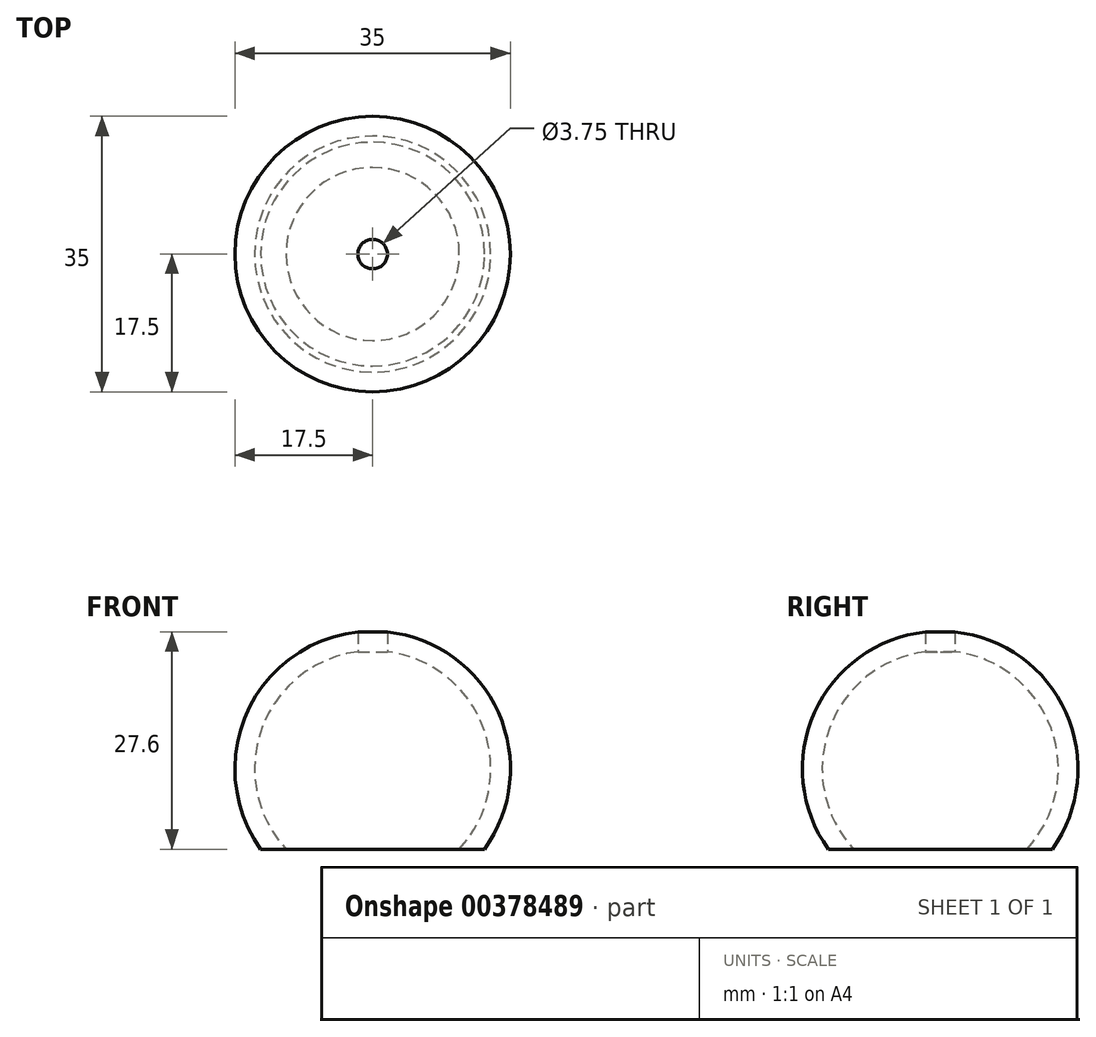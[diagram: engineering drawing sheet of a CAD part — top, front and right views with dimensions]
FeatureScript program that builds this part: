
annotation { "Feature Type Name" : "Feature", "Feature Type Description" : "" }
export const myFeature = defineFeature(function(context is Context, id is Id, definition is map)
    precondition{}
    {
        {
            var Q0;
            Q0=qCreatedBy(makeId("Front.planeOp"),FACE);
            var sketch = newSketch(context, id + "F0", { "sketchPlane" : qUnion([Q0])});
            skArc(sketch, "E0", {"start": v(0, -17.5) * mm, "mid": v(17.5, 0) * mm, "end": v(0, 17.5) * mm});
            skLineSegment(sketch, "E1", {"start": v(0, 0) * mm, "end": v(0, -17.5) * mm});
            skLineSegment(sketch, "E2", {"start": v(0, 0) * mm, "end": v(0, 17.5) * mm});
            skSolve(sketch);
        }
        {
            var Q0;
            Q0=makeQuery(id+"F0.imprint","IMPRINT",FACE,{"disambiguationData":[TD([[makeQuery(id+"F0.imprint","IMPRINT",EDGE,{"derivedFrom":sQuery(id+"F0.wireOp",EDGE,"E0")}),1.0]])]});
            var Q1;
            Q1=sQuery(id+"F0.wireOp",EDGE,"E1");
            revolve(context, id + "F1", {"entities" : qUnion([Q0]), "axis" : qUnion([Q1]), "revolveType" : RevolveType.FULL});
        }
        {
            var Q0;
            Q0=qCreatedBy(makeId("Front.planeOp"),FACE);
            var sketch = newSketch(context, id + "F2", { "sketchPlane" : qUnion([Q0])});
            skArc(sketch, "E3", {"start": v(0, -15) * mm, "mid": v(15, 0) * mm, "end": v(0, 15) * mm});
            skLineSegment(sketch, "E4", {"start": v(0, 15) * mm, "end": v(0, -15) * mm});
            skSolve(sketch);
        }
        {
            var Q0;
            Q0=makeQuery(id+"F2.imprint","IMPRINT",FACE,{"disambiguationData":[TD([[makeQuery(id+"F2.imprint","IMPRINT",EDGE,{"derivedFrom":sQuery(id+"F2.wireOp",EDGE,"E3")}),1.0]])]});
            var Q1;
            Q1=sQuery(id+"F0.wireOp",EDGE,"E2");
            revolve(context, id + "F3", {"entities" : qUnion([Q0]), "axis" : qUnion([Q1]), "revolveType" : RevolveType.FULL});
        }
        {
            var Q0;
            Q0=makeQuery(id+"F3.opRevolve","SWEPT_BODY",BODY,{"disambiguationData":[OSD([sQuery(id+"F2.wireOp",EDGE,"E3"),sQuery(id+"F2.wireOp",EDGE,"E4")])]});
            var Q1;
            Q1=makeQuery(id+"F1.opRevolve","SWEPT_BODY",BODY,{"disambiguationData":[OSD([sQuery(id+"F0.wireOp",EDGE,"E0"),sQuery(id+"F0.wireOp",EDGE,"E1"),sQuery(id+"F0.wireOp",EDGE,"E2")])]});
            booleanBodies(context, id + "F4", {"operationType" : BooleanOperationType.SUBTRACTION, "tools" : qUnion([Q0]), "targets" : qUnion([Q1])});
        }
        {
            var Q0;
            Q0=qCreatedBy(makeId("Front.planeOp"),FACE);
            var sketch = newSketch(context, id + "F5", { "sketchPlane" : qUnion([Q0])});
            skLineSegment(sketch, "E5.bottom", {"start": v(-19.8, -21) * mm, "end": v(22.47, -21) * mm});
            skLineSegment(sketch, "E5.top", {"start": v(-19.8, -10.2) * mm, "end": v(22.47, -10.2) * mm});
            skLineSegment(sketch, "E5.left", {"start": v(-19.8, -21) * mm, "end": v(-19.8, -10.2) * mm});
            skLineSegment(sketch, "E5.right", {"start": v(22.47, -21) * mm, "end": v(22.47, -10.2) * mm});
            skSolve(sketch);
        }
        {
            var Q0;
            Q0=makeQuery(id+"F5.imprint","IMPRINT",FACE,{"disambiguationData":[TD([[makeQuery(id+"F5.imprint","IMPRINT",EDGE,{"derivedFrom":sQuery(id+"F5.wireOp",EDGE,"E5.bottom")}),1.0]])]});
            extrude(context, id + "F6", {"entities" : qUnion([Q0]), "operationType" : NewBodyOperationType.REMOVE, "endBound" : BoundingType.SYMMETRIC, "oppositeDirection" : true, "depth" : 60 * mm});
        }
        {
            var Q0;
            Q0=qCreatedBy(makeId("Top.planeOp"),FACE);
            var sketch = newSketch(context, id + "F7", { "sketchPlane" : qUnion([Q0])});
            skCircle(sketch, "E6", {"center": v(0, 0) * mm, "radius": 1.88 * mm});
            skSolve(sketch);
        }
        {
            var Q0;
            Q0=makeQuery(id+"F7.imprint","IMPRINT",FACE,{"disambiguationData":[TD([[makeQuery(id+"F7.imprint","IMPRINT",EDGE,{"derivedFrom":sQuery(id+"F7.wireOp",EDGE,"E6")}),1.0]])]});
            extrude(context, id + "F8", {"entities" : qUnion([Q0]), "operationType" : NewBodyOperationType.REMOVE, "depth" : 25 * mm});
        }
    });
